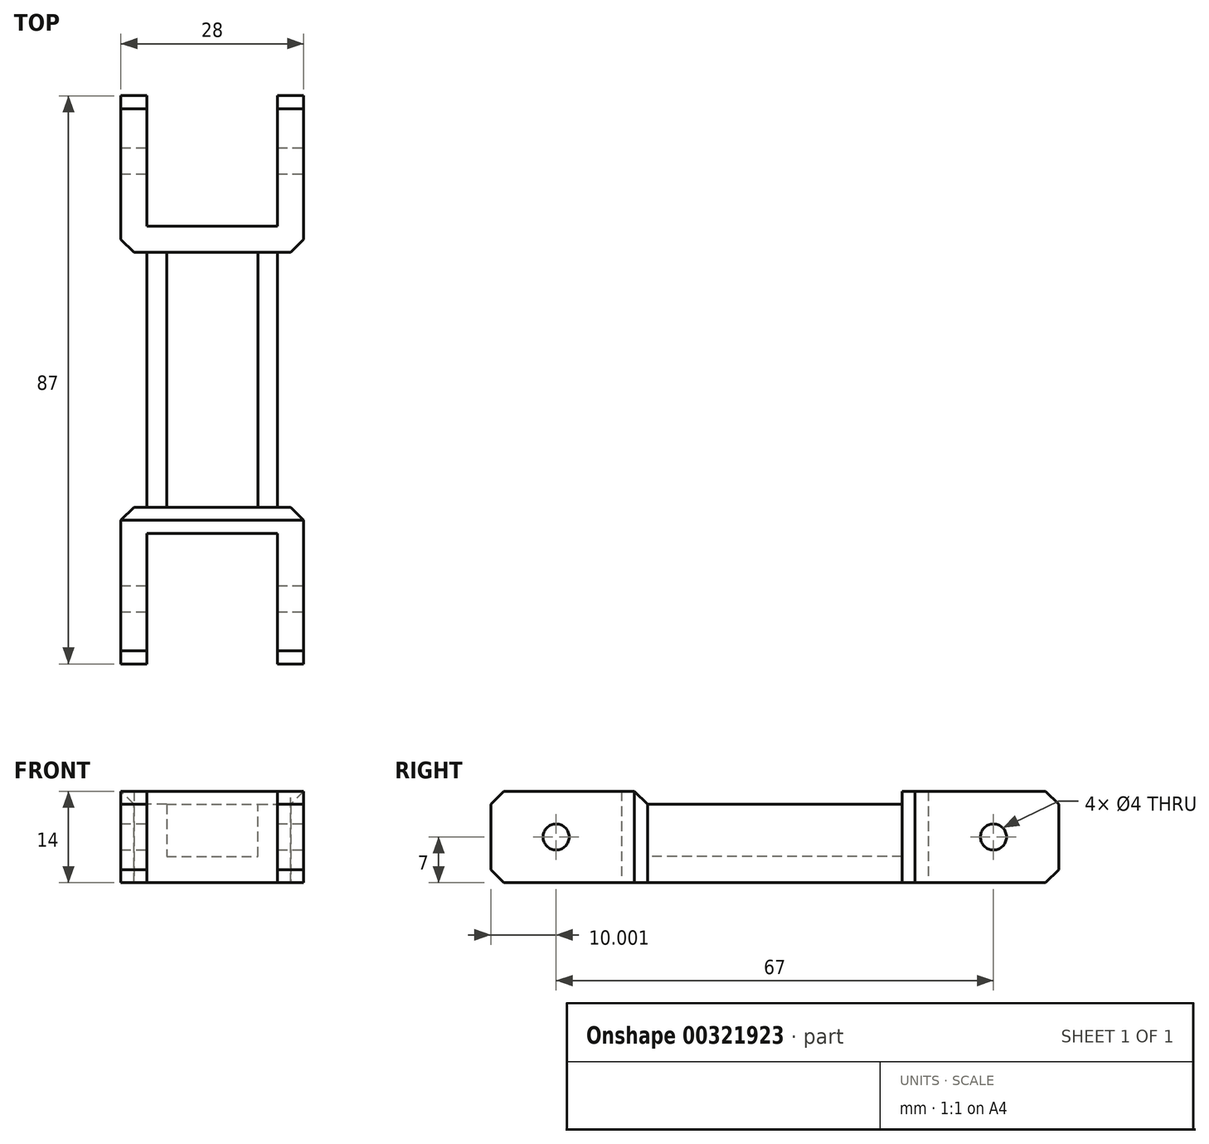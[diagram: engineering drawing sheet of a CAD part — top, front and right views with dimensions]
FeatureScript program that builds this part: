
annotation { "Feature Type Name" : "Feature", "Feature Type Description" : "" }
export const myFeature = defineFeature(function(context is Context, id is Id, definition is map)
    precondition{}
    {
        {
            var Q0;
            Q0=qCreatedBy(makeId("Top.planeOp"),FACE);
            var sketch = newSketch(context, id + "F0", { "sketchPlane" : qUnion([Q0])});
            skLineSegment(sketch, "E0.bottom", {"start": v(-54.4, 33.69) * mm, "end": v(-34.4, 33.69) * mm});
            skLineSegment(sketch, "E0.top", {"start": v(-54.4, 13.29) * mm, "end": v(-34.4, 13.29) * mm});
            skLineSegment(sketch, "E0.left", {"start": v(-54.4, 33.69) * mm, "end": v(-54.4, 13.29) * mm});
            skLineSegment(sketch, "E0.right", {"start": v(-34.4, 33.69) * mm, "end": v(-34.4, 13.29) * mm});
            skLineSegment(sketch, "E1.bottom", {"start": v(-54.4, 63.69) * mm, "end": v(-34.4, 63.69) * mm});
            skLineSegment(sketch, "E1.top", {"start": v(-54.4, 9.29) * mm, "end": v(-34.4, 9.29) * mm});
            skLineSegment(sketch, "E1.left", {"start": v(-54.4, 63.69) * mm, "end": v(-54.4, 9.29) * mm});
            skLineSegment(sketch, "E1.right", {"start": v(-34.4, 63.69) * mm, "end": v(-34.4, 9.29) * mm});
            skLineSegment(sketch, "E2", {"start": v(-54.4, 59.69) * mm, "end": v(-34.4, 59.69) * mm});
            skLineSegment(sketch, "E3", {"start": v(-54.4, 37.69) * mm, "end": v(-34.4, 37.69) * mm});
            skSolve(sketch);
        }
        {
            var Q0;
            {var subQ0=sQuery(id+"F0.wireOp",EDGE,"E2");Q0=makeQuery(id+"F0.imprint","IMPRINT",FACE,{"disambiguationData":[TD([[makeQuery(id+"F0.imprint","IMPRINT",EDGE,{"derivedFrom":subQ0}),-1.0]])]});}
            var Q1;
            {var subQ0=sQuery(id+"F0.wireOp",EDGE,"E1.bottom");Q1=makeQuery(id+"F0.imprint","IMPRINT",FACE,{"disambiguationData":[TD([[makeQuery(id+"F0.imprint","IMPRINT",EDGE,{"derivedFrom":subQ0}),-1.0]])]});}
            var Q2;
            Q2=makeQuery(id+"F0.imprint","IMPRINT",FACE,{"disambiguationData":[TD([[makeQuery(id+"F0.imprint","IMPRINT",EDGE,{"derivedFrom":sQuery(id+"F0.wireOp",EDGE,"E0.bottom")}),1.0]])]});
            var Q3;
            {var subQ0=sQuery(id+"F0.wireOp",EDGE,"E0.bottom");Q3=makeQuery(id+"F0.imprint","IMPRINT",FACE,{"disambiguationData":[TD([[makeQuery(id+"F0.imprint","IMPRINT",EDGE,{"derivedFrom":subQ0}),-1.0]])]});}
            var Q4;
            {var subQ0=sQuery(id+"F0.wireOp",EDGE,"E0.top");Q4=makeQuery(id+"F0.imprint","IMPRINT",FACE,{"disambiguationData":[TD([[makeQuery(id+"F0.imprint","IMPRINT",EDGE,{"derivedFrom":subQ0}),-1.0]])]});}
            extrude(context, id + "F1", {"entities" : qUnion([Q0, Q1, Q2, Q3, Q4]), "oppositeDirection" : true, "depth" : 2 * mm});
        }
        {
            var Q0;
            Q0=makeQuery(id+"F0.imprint","IMPRINT",FACE,{"disambiguationData":[TD([[makeQuery(id+"F0.imprint","IMPRINT",EDGE,{"derivedFrom":sQuery(id+"F0.wireOp",EDGE,"E0.bottom")}),1.0]])]});
            var Q1;
            {var subQ0=sQuery(id+"F0.wireOp",EDGE,"E1.bottom");Q1=makeQuery(id+"F0.imprint","IMPRINT",FACE,{"disambiguationData":[TD([[makeQuery(id+"F0.imprint","IMPRINT",EDGE,{"derivedFrom":subQ0}),-1.0]])]});}
            var Q2;
            {var subQ0=sQuery(id+"F0.wireOp",EDGE,"E0.top");Q2=makeQuery(id+"F0.imprint","IMPRINT",FACE,{"disambiguationData":[TD([[makeQuery(id+"F0.imprint","IMPRINT",EDGE,{"derivedFrom":subQ0}),-1.0]])]});}
            extrude(context, id + "F2", {"entities" : qUnion([Q0, Q1, Q2]), "operationType" : NewBodyOperationType.ADD, "depth" : 10 * mm});
        }
        {
            var Q0;
            {var subQ0=sQuery(id+"F0.wireOp",EDGE,"E1.top");Q0=makeQuery(id+"F2.boolean.opBoolean","MERGE",FACE,{"derivedFrom":[makeQuery(id+"F1.opExtrude","SWEPT_FACE",FACE,{"disambiguationData":[OSD([subQ0])]}),makeQuery(id+"F2.opExtrude","SWEPT_FACE",FACE,{"disambiguationData":[OSD([subQ0])]})]});}
            var sketch = newSketch(context, id + "F3", { "sketchPlane" : qUnion([Q0])});
            skCircle(sketch, "E4", {"center": v(-44.4, 5.5) * mm, "radius": 2.2 * mm});
            skPoint(sketch, "E4.centerSnap0", {"position": v(-44.4, -2) * mm});
            skSolve(sketch);
        }
        {
            var Q0;
            Q0=makeQuery(id+"F3.imprint","IMPRINT",FACE,{"disambiguationData":[TD([[makeQuery(id+"F3.imprint","IMPRINT",EDGE,{"derivedFrom":sQuery(id+"F3.wireOp",EDGE,"E4")}),1.0]])]});
            extrude(context, id + "F4", {"entities" : qUnion([Q0]), "operationType" : NewBodyOperationType.REMOVE, "oppositeDirection" : true, "depth" : 30 * mm, "offsetDistance" : 25 * mm});
        }
        {
            var Q0;
            {var subQ0=sQuery(id+"F0.wireOp",EDGE,"E1.left");Q0=makeQuery(id+"F2.boolean.opBoolean","MERGE",FACE,{"derivedFrom":[makeQuery(id+"F1.opExtrude","SWEPT_FACE",FACE,{"disambiguationData":[OSD([subQ0])]}),makeQuery(id+"F2.opExtrude","SWEPT_FACE",FACE,{"disambiguationData":[OSD([subQ0]),TDD([makeQuery(id+"F0.imprint","IMPRINT",EDGE,{"disambiguationData":[TD([[makeQuery(id+"F0.imprint","INTERSECT",VERTEX,{"derivedFrom":[sQuery(id+"F0.wireOp",EDGE,"E1.bottom"),subQ0]}),-1.0]])],"derivedFrom":subQ0})])]}),makeQuery(id+"F2.opExtrude","SWEPT_FACE",FACE,{"disambiguationData":[OSD([subQ0]),TDD([makeQuery(id+"F0.imprint","IMPRINT",EDGE,{"disambiguationData":[TD([[makeQuery(id+"F0.imprint","INTERSECT",VERTEX,{"derivedFrom":[sQuery(id+"F0.wireOp",EDGE,"E0.bottom"),subQ0]}),1.0]])],"derivedFrom":subQ0})])]}),makeQuery(id+"F2.opExtrude","SWEPT_FACE",FACE,{"disambiguationData":[OSD([subQ0]),TDD([makeQuery(id+"F0.imprint","IMPRINT",EDGE,{"disambiguationData":[TD([[makeQuery(id+"F0.imprint","INTERSECT",VERTEX,{"derivedFrom":[sQuery(id+"F0.wireOp",EDGE,"E0.top"),subQ0]}),-1.0]])],"derivedFrom":subQ0})])]})]});}
            var sketch = newSketch(context, id + "F5", { "sketchPlane" : qUnion([Q0])});
            skLineSegment(sketch, "E5.bottom", {"start": v(-59.69, 10) * mm, "end": v(-83.69, 10) * mm});
            skLineSegment(sketch, "E5.top", {"start": v(-59.69, -2) * mm, "end": v(-83.69, -2) * mm});
            skLineSegment(sketch, "E5.left", {"start": v(-59.69, 10) * mm, "end": v(-59.69, -2) * mm});
            skLineSegment(sketch, "E5.right", {"start": v(-83.69, 10) * mm, "end": v(-83.69, -2) * mm});
            skCircle(sketch, "E6", {"center": v(-73.69, 4) * mm, "radius": 2.6 * mm});
            skPoint(sketch, "E6.centerSnap0", {"position": v(-83.69, 4) * mm});
            skSolve(sketch);
        }
        {
            var Q0;
            {var subQ0=sQuery(id+"F0.wireOp",EDGE,"E1.right");Q0=makeQuery(id+"F2.boolean.opBoolean","MERGE",FACE,{"derivedFrom":[makeQuery(id+"F1.opExtrude","SWEPT_FACE",FACE,{"disambiguationData":[OSD([subQ0])]}),makeQuery(id+"F2.opExtrude","SWEPT_FACE",FACE,{"disambiguationData":[OSD([subQ0]),TDD([makeQuery(id+"F0.imprint","IMPRINT",EDGE,{"disambiguationData":[TD([[makeQuery(id+"F0.imprint","INTERSECT",VERTEX,{"derivedFrom":[sQuery(id+"F0.wireOp",EDGE,"E1.bottom"),subQ0]}),-1.0]])],"derivedFrom":subQ0})])]}),makeQuery(id+"F2.opExtrude","SWEPT_FACE",FACE,{"disambiguationData":[OSD([subQ0]),TDD([makeQuery(id+"F0.imprint","IMPRINT",EDGE,{"disambiguationData":[TD([[makeQuery(id+"F0.imprint","INTERSECT",VERTEX,{"derivedFrom":[sQuery(id+"F0.wireOp",EDGE,"E0.bottom"),subQ0]}),1.0]])],"derivedFrom":subQ0})])]}),makeQuery(id+"F2.opExtrude","SWEPT_FACE",FACE,{"disambiguationData":[OSD([subQ0]),TDD([makeQuery(id+"F0.imprint","IMPRINT",EDGE,{"disambiguationData":[TD([[makeQuery(id+"F0.imprint","INTERSECT",VERTEX,{"derivedFrom":[sQuery(id+"F0.wireOp",EDGE,"E0.top"),subQ0]}),-1.0]])],"derivedFrom":subQ0})])]})]});}
            var sketch = newSketch(context, id + "F6", { "sketchPlane" : qUnion([Q0])});
            skLineSegment(sketch, "E7.bottom", {"start": v(59.69, 10) * mm, "end": v(83.69, 10) * mm});
            skLineSegment(sketch, "E7.top", {"start": v(59.69, -2) * mm, "end": v(83.69, -2) * mm});
            skLineSegment(sketch, "E7.left", {"start": v(59.69, 10) * mm, "end": v(59.69, -2) * mm});
            skLineSegment(sketch, "E7.right", {"start": v(83.69, 10) * mm, "end": v(83.69, -2) * mm});
            skCircle(sketch, "E8", {"center": v(73.69, 4) * mm, "radius": 2.6 * mm});
            skPoint(sketch, "E8.centerSnap0", {"position": v(83.69, 4) * mm});
            skSolve(sketch);
        }
        {
            var Q0;
            {var subQ4=sQuery(id+"F5.wireOp",EDGE,"E5.right");Q0=makeQuery(id+"F5.imprint","IMPRINT",FACE,{"disambiguationData":[TD([[makeQuery(id+"F5.imprint","IMPRINT",EDGE,{"derivedFrom":subQ4}),1.0]])]});}
            var Q1;
            {var subQ3=sQuery(id+"F0.wireOp",EDGE,"E1.left");var subQ5=sQuery(id+"F0.wireOp",EDGE,"E1.bottom");var subQ10=makeQuery(id+"F2.boolean.opBoolean","MERGE",EDGE,{"derivedFrom":[makeQuery(id+"F1.opExtrude","SWEPT_EDGE",EDGE,{"disambiguationData":[OSD([subQ5,subQ3])]}),makeQuery(id+"F2.opExtrude","SWEPT_EDGE",EDGE,{"disambiguationData":[OSD([subQ5,subQ3])]})]});Q1=makeQuery(id+"F5.imprint","IMPRINT",FACE,{"disambiguationData":[TD([[makeQuery(id+"F5.imprint","IMPRINT",EDGE,{"derivedFrom":subQ10}),-1.0]])]});}
            extrude(context, id + "F7", {"entities" : qUnion([Q0, Q1]), "operationType" : NewBodyOperationType.ADD, "depth" : 4 * mm});
        }
        {
            var Q0;
            {var subQ0=sQuery(id+"F5.wireOp",EDGE,"As3iJ9jp-MM02-xgW6-gQvA-6wpTA8jTOXIw.right");Q0=makeQuery(id+"F5.imprint","IMPRINT",FACE,{"disambiguationData":[TD([[makeQuery(id+"F5.imprint","IMPRINT",EDGE,{"derivedFrom":subQ0}),-1.0]])]});}
            var Q1;
            {var subQ5=sQuery(id+"F5.wireOp",EDGE,"D0sxENBk-QWaU-MoL9-KmcH-z9rnvNsLjtkH");Q1=makeQuery(id+"F5.imprint","IMPRINT",FACE,{"disambiguationData":[TD([[makeQuery(id+"F5.imprint","IMPRINT",EDGE,{"derivedFrom":subQ5}),-1.0]])]});}
            var Q2;
            {var subQ4=sQuery(id+"F6.wireOp",EDGE,"E7.right");Q2=makeQuery(id+"F6.imprint","IMPRINT",FACE,{"disambiguationData":[TD([[makeQuery(id+"F6.imprint","IMPRINT",EDGE,{"derivedFrom":subQ4}),-1.0]])]});}
            var Q3;
            {var subQ3=sQuery(id+"F0.wireOp",EDGE,"E1.right");var subQ4=sQuery(id+"F0.wireOp",EDGE,"E1.bottom");var subQ10=makeQuery(id+"F2.boolean.opBoolean","MERGE",EDGE,{"derivedFrom":[makeQuery(id+"F1.opExtrude","SWEPT_EDGE",EDGE,{"disambiguationData":[OSD([subQ4,subQ3])]}),makeQuery(id+"F2.opExtrude","SWEPT_EDGE",EDGE,{"disambiguationData":[OSD([subQ4,subQ3])]})]});Q3=makeQuery(id+"F6.imprint","IMPRINT",FACE,{"disambiguationData":[TD([[makeQuery(id+"F6.imprint","IMPRINT",EDGE,{"derivedFrom":subQ10}),1.0]])]});}
            extrude(context, id + "F8", {"entities" : qUnion([Q0, Q1, Q2, Q3]), "operationType" : NewBodyOperationType.ADD, "depth" : 4 * mm});
        }
        {
            var Q0;
            Q0=makeQuery(id+"F8.boolean.opBoolean","MERGE",FACE,{"derivedFrom":[makeQuery(id+"F7.boolean.opBoolean","MERGE",FACE,{"derivedFrom":[makeQuery(id+"F1.opExtrude","CAP_FACE",FACE,{"disambiguationData":[OSD([sQuery(id+"F0.wireOp",EDGE,"E1.bottom"),sQuery(id+"F0.wireOp",EDGE,"E1.top"),sQuery(id+"F0.wireOp",EDGE,"E1.left"),sQuery(id+"F0.wireOp",EDGE,"E1.right")])],"isStart":false}),makeQuery(id+"F7.opExtrude","SWEPT_FACE",FACE,{"disambiguationData":[OSD([sQuery(id+"F5.wireOp",EDGE,"E5.top")])]})]}),makeQuery(id+"F8.opExtrude","SWEPT_FACE",FACE,{"disambiguationData":[OSD([sQuery(id+"F6.wireOp",EDGE,"E7.top")])]})]});
            var Q1;
            Q1=makeQuery(id+"F8.boolean.opBoolean","MERGE",FACE,{"derivedFrom":[makeQuery(id+"F7.boolean.opBoolean","MERGE",FACE,{"derivedFrom":[makeQuery(id+"F2.opExtrude","CAP_FACE",FACE,{"disambiguationData":[OSD([sQuery(id+"F0.wireOp",EDGE,"E1.bottom"),sQuery(id+"F0.wireOp",EDGE,"E1.left"),sQuery(id+"F0.wireOp",EDGE,"E1.right"),sQuery(id+"F0.wireOp",EDGE,"E2")])],"isStart":false}),makeQuery(id+"F7.opExtrude","SWEPT_FACE",FACE,{"disambiguationData":[OSD([sQuery(id+"F5.wireOp",EDGE,"E5.bottom")])]})]}),makeQuery(id+"F8.opExtrude","SWEPT_FACE",FACE,{"disambiguationData":[OSD([sQuery(id+"F6.wireOp",EDGE,"E7.bottom")])]})]});
            var Q2;
            Q2=makeQuery(id+"F2.opExtrude","CAP_FACE",FACE,{"disambiguationData":[OSD([sQuery(id+"F0.wireOp",EDGE,"E0.bottom"),sQuery(id+"F0.wireOp",EDGE,"E1.left"),sQuery(id+"F0.wireOp",EDGE,"E1.right"),sQuery(id+"F0.wireOp",EDGE,"E3")])],"isStart":false});
            var Q3;
            Q3=makeQuery(id+"F2.opExtrude","CAP_FACE",FACE,{"disambiguationData":[OSD([sQuery(id+"F0.wireOp",EDGE,"E0.top"),sQuery(id+"F0.wireOp",EDGE,"E1.top"),sQuery(id+"F0.wireOp",EDGE,"E1.left"),sQuery(id+"F0.wireOp",EDGE,"E1.right")])],"isStart":false});
            var Q4;
            {var subQ0=sQuery(id+"F0.wireOp",EDGE,"E1.right");var subQ1=sQuery(id+"F0.wireOp",EDGE,"E1.top");Q4=makeQuery(id+"F2.boolean.opBoolean","MERGE",EDGE,{"derivedFrom":[makeQuery(id+"F1.opExtrude","SWEPT_EDGE",EDGE,{"disambiguationData":[OSD([subQ1,subQ0])]}),makeQuery(id+"F2.opExtrude","SWEPT_EDGE",EDGE,{"disambiguationData":[OSD([subQ1,subQ0])]})]});}
            var Q5;
            {var subQ0=sQuery(id+"F0.wireOp",EDGE,"E1.left");var subQ1=sQuery(id+"F0.wireOp",EDGE,"E1.top");Q5=makeQuery(id+"F2.boolean.opBoolean","MERGE",EDGE,{"derivedFrom":[makeQuery(id+"F1.opExtrude","SWEPT_EDGE",EDGE,{"disambiguationData":[OSD([subQ1,subQ0])]}),makeQuery(id+"F2.opExtrude","SWEPT_EDGE",EDGE,{"disambiguationData":[OSD([subQ1,subQ0])]})]});}
            var Q6;
            Q6=makeQuery(id+"F7.opExtrude","CAP_EDGE",EDGE,{"disambiguationData":[OSD([sQuery(id+"F5.wireOp",EDGE,"E5.left")])],"isStart":false});
            var Q7;
            Q7=makeQuery(id+"F8.opExtrude","CAP_EDGE",EDGE,{"disambiguationData":[OSD([sQuery(id+"F6.wireOp",EDGE,"E7.left")])],"isStart":false});
            var Q8;
            Q8=makeQuery(id+"F8.opExtrude","CAP_EDGE",EDGE,{"disambiguationData":[OSD([sQuery(id+"F6.wireOp",EDGE,"E7.right")])],"isStart":false});
            var Q9;
            Q9=makeQuery(id+"F7.opExtrude","CAP_EDGE",EDGE,{"disambiguationData":[OSD([sQuery(id+"F5.wireOp",EDGE,"E5.right")])],"isStart":false});
            fillet(context, id + "F9", {"entities" : qUnion([Q0, Q1, Q2, Q3, Q4, Q5, Q6, Q7, Q8, Q9]), "radius" : 2 * mm, "allowEdgeOverflow" : false});
        }
        {
            var Q0;
            Q0=qCreatedBy(makeId("Top.planeOp"),FACE);
            var sketch = newSketch(context, id + "F10", { "sketchPlane" : qUnion([Q0])});
            skLineSegment(sketch, "E9.bottom", {"start": v(-54.07, -34.84) * mm, "end": v(-34.07, -34.84) * mm});
            skLineSegment(sketch, "E9.top", {"start": v(-54.07, -81.84) * mm, "end": v(-34.07, -81.84) * mm});
            skLineSegment(sketch, "E9.left", {"start": v(-54.07, -34.84) * mm, "end": v(-54.07, -81.84) * mm});
            skLineSegment(sketch, "E9.right", {"start": v(-34.07, -34.84) * mm, "end": v(-34.07, -81.84) * mm});
            skSolve(sketch);
        }
        {
            var Q0;
            Q0 = qSketchRegion(id + "F10", true);
            extrude(context, id + "F11", {"entities" : qUnion([Q0]), "depth" : 4 * mm, "offsetDistance" : 25 * mm});
        }
        {
            var Q0;
            Q0=makeQuery(id+"F11.opExtrude","CAP_FACE",FACE,{"disambiguationData":[OSD([sQuery(id+"F10.wireOp",EDGE,"E9.bottom"),sQuery(id+"F10.wireOp",EDGE,"E9.top"),sQuery(id+"F10.wireOp",EDGE,"E9.left"),sQuery(id+"F10.wireOp",EDGE,"E9.right")])],"isStart":false});
            var sketch = newSketch(context, id + "F12", { "sketchPlane" : qUnion([Q0])});
            skLineSegment(sketch, "E10", {"start": v(-54.07, -38.84) * mm, "end": v(-34.07, -38.84) * mm});
            skLineSegment(sketch, "E11", {"start": v(-54.07, -77.84) * mm, "end": v(-34.07, -77.84) * mm});
            skSolve(sketch);
        }
        {
            var Q0;
            {var subQ0=sQuery(id+"F12.wireOp",EDGE,"E10");Q0=makeQuery(id+"F12.imprint","IMPRINT",FACE,{"disambiguationData":[TD([[makeQuery(id+"F12.imprint","IMPRINT",EDGE,{"derivedFrom":subQ0}),1.0]])]});}
            var Q1;
            {var subQ0=sQuery(id+"F12.wireOp",EDGE,"E11");Q1=makeQuery(id+"F12.imprint","IMPRINT",FACE,{"disambiguationData":[TD([[makeQuery(id+"F12.imprint","IMPRINT",EDGE,{"derivedFrom":subQ0}),-1.0]])]});}
            extrude(context, id + "F13", {"entities" : qUnion([Q0, Q1]), "operationType" : NewBodyOperationType.ADD, "depth" : 10 * mm, "offsetDistance" : 25 * mm});
        }
        {
            var Q0;
            {var subQ0=sQuery(id+"F10.wireOp",EDGE,"E9.left");var subQ1=makeQuery(id+"F11.opExtrude","CAP_EDGE",EDGE,{"disambiguationData":[OSD([subQ0])],"isStart":false});Q0=makeQuery(id+"F13.boolean.opBoolean","MERGE",FACE,{"derivedFrom":[makeQuery(id+"F11.opExtrude","SWEPT_FACE",FACE,{"disambiguationData":[OSD([subQ0])]}),makeQuery(id+"F13.opExtrude","SWEPT_FACE",FACE,{"disambiguationData":[OSD([subQ0]),TDD([makeQuery(id+"F12.imprint","IMPRINT",EDGE,{"disambiguationData":[TD([[makeQuery(id+"F12.imprint","INTERSECT",VERTEX,{"derivedFrom":[makeQuery(id+"F11.opExtrude","CAP_EDGE",EDGE,{"disambiguationData":[OSD([sQuery(id+"F10.wireOp",EDGE,"E9.bottom")])],"isStart":false}),subQ1]}),-1.0]])],"derivedFrom":subQ1})])]}),makeQuery(id+"F13.opExtrude","SWEPT_FACE",FACE,{"disambiguationData":[OSD([subQ0]),TDD([makeQuery(id+"F12.imprint","IMPRINT",EDGE,{"disambiguationData":[TD([[makeQuery(id+"F12.imprint","INTERSECT",VERTEX,{"derivedFrom":[makeQuery(id+"F11.opExtrude","CAP_EDGE",EDGE,{"disambiguationData":[OSD([sQuery(id+"F10.wireOp",EDGE,"E9.top")])],"isStart":false}),subQ1]}),1.0]])],"derivedFrom":subQ1})])]})]});}
            var sketch = newSketch(context, id + "F14", { "sketchPlane" : qUnion([Q0])});
            skLineSegment(sketch, "E12", {"start": v(38.84, 4) * mm, "end": v(38.84, 0) * mm});
            skLineSegment(sketch, "E13", {"start": v(77.84, 4) * mm, "end": v(77.84, 0) * mm});
            skSolve(sketch);
        }
        {
            var Q0;
            {var subQ0=sQuery(id+"F10.wireOp",EDGE,"E9.right");var subQ1=makeQuery(id+"F11.opExtrude","CAP_EDGE",EDGE,{"disambiguationData":[OSD([subQ0])],"isStart":false});Q0=makeQuery(id+"F13.boolean.opBoolean","MERGE",FACE,{"derivedFrom":[makeQuery(id+"F11.opExtrude","SWEPT_FACE",FACE,{"disambiguationData":[OSD([subQ0])]}),makeQuery(id+"F13.opExtrude","SWEPT_FACE",FACE,{"disambiguationData":[OSD([subQ0]),TDD([makeQuery(id+"F12.imprint","IMPRINT",EDGE,{"disambiguationData":[TD([[makeQuery(id+"F12.imprint","INTERSECT",VERTEX,{"derivedFrom":[makeQuery(id+"F11.opExtrude","CAP_EDGE",EDGE,{"disambiguationData":[OSD([sQuery(id+"F10.wireOp",EDGE,"E9.bottom")])],"isStart":false}),subQ1]}),-1.0]])],"derivedFrom":subQ1})])]}),makeQuery(id+"F13.opExtrude","SWEPT_FACE",FACE,{"disambiguationData":[OSD([subQ0]),TDD([makeQuery(id+"F12.imprint","IMPRINT",EDGE,{"disambiguationData":[TD([[makeQuery(id+"F12.imprint","INTERSECT",VERTEX,{"derivedFrom":[makeQuery(id+"F11.opExtrude","CAP_EDGE",EDGE,{"disambiguationData":[OSD([sQuery(id+"F10.wireOp",EDGE,"E9.top")])],"isStart":false}),subQ1]}),1.0]])],"derivedFrom":subQ1})])]})]});}
            var sketch = newSketch(context, id + "F15", { "sketchPlane" : qUnion([Q0])});
            skLineSegment(sketch, "E14", {"start": v(-77.84, 4) * mm, "end": v(-77.84, 0) * mm});
            skLineSegment(sketch, "E15", {"start": v(-38.84, 4) * mm, "end": v(-38.84, 0) * mm});
            skSolve(sketch);
        }
        {
            var Q0;
            {var subQ5=sQuery(id+"F15.wireOp",EDGE,"E14");Q0=makeQuery(id+"F15.imprint","IMPRINT",FACE,{"disambiguationData":[TD([[makeQuery(id+"F15.imprint","IMPRINT",EDGE,{"derivedFrom":subQ5}),-1.0]])]});}
            var Q1;
            {var subQ5=sQuery(id+"F15.wireOp",EDGE,"E15");Q1=makeQuery(id+"F15.imprint","IMPRINT",FACE,{"disambiguationData":[TD([[makeQuery(id+"F15.imprint","IMPRINT",EDGE,{"derivedFrom":subQ5}),1.0]])]});}
            extrude(context, id + "F16", {"entities" : qUnion([Q0, Q1]), "operationType" : NewBodyOperationType.ADD, "depth" : 4 * mm, "offsetDistance" : 25 * mm});
        }
        {
            var Q0;
            {var subQ5=sQuery(id+"F14.wireOp",EDGE,"E12");Q0=makeQuery(id+"F14.imprint","IMPRINT",FACE,{"disambiguationData":[TD([[makeQuery(id+"F14.imprint","IMPRINT",EDGE,{"derivedFrom":subQ5}),-1.0]])]});}
            var Q1;
            {var subQ5=sQuery(id+"F14.wireOp",EDGE,"E13");Q1=makeQuery(id+"F14.imprint","IMPRINT",FACE,{"disambiguationData":[TD([[makeQuery(id+"F14.imprint","IMPRINT",EDGE,{"derivedFrom":subQ5}),1.0]])]});}
            extrude(context, id + "F17", {"entities" : qUnion([Q0, Q1]), "operationType" : NewBodyOperationType.ADD, "depth" : 4 * mm, "offsetDistance" : 25 * mm});
        }
        {
            var Q0;
            {var subQ0=sQuery(id+"F10.wireOp",EDGE,"E9.bottom");Q0=makeQuery(id+"F17.boolean.opBoolean","MERGE",FACE,{"derivedFrom":[makeQuery(id+"F16.boolean.opBoolean","MERGE",FACE,{"derivedFrom":[makeQuery(id+"F13.boolean.opBoolean","MERGE",FACE,{"derivedFrom":[makeQuery(id+"F11.opExtrude","SWEPT_FACE",FACE,{"disambiguationData":[OSD([subQ0])]}),makeQuery(id+"F13.opExtrude","SWEPT_FACE",FACE,{"disambiguationData":[OSD([subQ0])]})]}),makeQuery(id+"F16.opExtrude","SWEPT_FACE",FACE,{"disambiguationData":[OSD([subQ0,sQuery(id+"F10.wireOp",EDGE,"E9.right")])]})]}),makeQuery(id+"F17.opExtrude","SWEPT_FACE",FACE,{"disambiguationData":[OSD([subQ0,sQuery(id+"F10.wireOp",EDGE,"E9.left")])]})]});}
            var sketch = newSketch(context, id + "F18", { "sketchPlane" : qUnion([Q0])});
            skLineSegment(sketch, "E16", {"start": v(34.07, 14) * mm, "end": v(34.07, 0) * mm});
            skLineSegment(sketch, "E17", {"start": v(54.07, 14) * mm, "end": v(54.07, 0) * mm});
            skSolve(sketch);
        }
        {
            var Q0;
            {var subQ0=sQuery(id+"F10.wireOp",EDGE,"E9.top");Q0=makeQuery(id+"F17.boolean.opBoolean","MERGE",FACE,{"derivedFrom":[makeQuery(id+"F16.boolean.opBoolean","MERGE",FACE,{"derivedFrom":[makeQuery(id+"F13.boolean.opBoolean","MERGE",FACE,{"derivedFrom":[makeQuery(id+"F11.opExtrude","SWEPT_FACE",FACE,{"disambiguationData":[OSD([subQ0])]}),makeQuery(id+"F13.opExtrude","SWEPT_FACE",FACE,{"disambiguationData":[OSD([subQ0])]})]}),makeQuery(id+"F16.opExtrude","SWEPT_FACE",FACE,{"disambiguationData":[OSD([subQ0,sQuery(id+"F10.wireOp",EDGE,"E9.right")])]})]}),makeQuery(id+"F17.opExtrude","SWEPT_FACE",FACE,{"disambiguationData":[OSD([subQ0,sQuery(id+"F10.wireOp",EDGE,"E9.left")])]})]});}
            var sketch = newSketch(context, id + "F19", { "sketchPlane" : qUnion([Q0])});
            skLineSegment(sketch, "E18", {"start": v(-54.07, 14) * mm, "end": v(-54.07, 0) * mm});
            skLineSegment(sketch, "E19", {"start": v(-34.07, 14) * mm, "end": v(-34.07, 0) * mm});
            skSolve(sketch);
        }
        {
            var Q0;
            {var subQ0=sQuery(id+"F19.wireOp",EDGE,"E18");Q0=makeQuery(id+"F19.imprint","IMPRINT",FACE,{"disambiguationData":[TD([[makeQuery(id+"F19.imprint","IMPRINT",EDGE,{"derivedFrom":subQ0}),-1.0]])]});}
            var Q1;
            {var subQ0=sQuery(id+"F19.wireOp",EDGE,"E19");Q1=makeQuery(id+"F19.imprint","IMPRINT",FACE,{"disambiguationData":[TD([[makeQuery(id+"F19.imprint","IMPRINT",EDGE,{"derivedFrom":subQ0}),1.0]])]});}
            extrude(context, id + "F20", {"entities" : qUnion([Q0, Q1]), "operationType" : NewBodyOperationType.ADD, "depth" : 20 * mm, "offsetDistance" : 25 * mm});
        }
        {
            var Q0;
            {var subQ0=sQuery(id+"F18.wireOp",EDGE,"E16");Q0=makeQuery(id+"F18.imprint","IMPRINT",FACE,{"disambiguationData":[TD([[makeQuery(id+"F18.imprint","IMPRINT",EDGE,{"derivedFrom":subQ0}),-1.0]])]});}
            var Q1;
            {var subQ0=sQuery(id+"F18.wireOp",EDGE,"E17");Q1=makeQuery(id+"F18.imprint","IMPRINT",FACE,{"disambiguationData":[TD([[makeQuery(id+"F18.imprint","IMPRINT",EDGE,{"derivedFrom":subQ0}),1.0]])]});}
            extrude(context, id + "F21", {"entities" : qUnion([Q0, Q1]), "operationType" : NewBodyOperationType.ADD, "depth" : 20 * mm, "offsetDistance" : 25 * mm});
        }
        {
            var Q0;
            {var subQ0=sQuery(id+"F10.wireOp",EDGE,"E9.left");var subQ1=makeQuery(id+"F11.opExtrude","CAP_EDGE",EDGE,{"disambiguationData":[OSD([subQ0])],"isStart":false});Q0=makeQuery(id+"F13.boolean.opBoolean","MERGE",FACE,{"derivedFrom":[makeQuery(id+"F11.opExtrude","SWEPT_FACE",FACE,{"disambiguationData":[OSD([subQ0])]}),makeQuery(id+"F13.opExtrude","SWEPT_FACE",FACE,{"disambiguationData":[OSD([subQ0]),TDD([makeQuery(id+"F12.imprint","IMPRINT",EDGE,{"disambiguationData":[TD([[makeQuery(id+"F12.imprint","INTERSECT",VERTEX,{"derivedFrom":[makeQuery(id+"F11.opExtrude","CAP_EDGE",EDGE,{"disambiguationData":[OSD([sQuery(id+"F10.wireOp",EDGE,"E9.bottom")])],"isStart":false}),subQ1]}),-1.0]])],"derivedFrom":subQ1})])]}),makeQuery(id+"F13.opExtrude","SWEPT_FACE",FACE,{"disambiguationData":[OSD([subQ0]),TDD([makeQuery(id+"F12.imprint","IMPRINT",EDGE,{"disambiguationData":[TD([[makeQuery(id+"F12.imprint","INTERSECT",VERTEX,{"derivedFrom":[makeQuery(id+"F11.opExtrude","CAP_EDGE",EDGE,{"disambiguationData":[OSD([sQuery(id+"F10.wireOp",EDGE,"E9.top")])],"isStart":false}),subQ1]}),1.0]])],"derivedFrom":subQ1})])]})]});}
            var sketch = newSketch(context, id + "F22", { "sketchPlane" : qUnion([Q0])});
            skLineSegment(sketch, "E20", {"start": v(38.84, 4) * mm, "end": v(38.84, 12) * mm});
            skLineSegment(sketch, "E21", {"start": v(38.84, 12) * mm, "end": v(77.84, 12) * mm});
            skLineSegment(sketch, "E22", {"start": v(77.84, 12) * mm, "end": v(77.84, 4) * mm});
            skLineSegment(sketch, "E23", {"start": v(77.84, 4) * mm, "end": v(38.84, 4) * mm});
            skSolve(sketch);
        }
        {
            var Q0;
            Q0=makeQuery(id+"F22.imprint","IMPRINT",FACE,{"disambiguationData":[TD([[makeQuery(id+"F22.imprint","IMPRINT",EDGE,{"derivedFrom":sQuery(id+"F22.wireOp",EDGE,"E20")}),-1.0]])]});
            extrude(context, id + "F23", {"entities" : qUnion([Q0]), "operationType" : NewBodyOperationType.ADD, "oppositeDirection" : true, "depth" : 3 * mm, "offsetDistance" : 25 * mm});
        }
        {
            var Q0;
            {var subQ0=sQuery(id+"F10.wireOp",EDGE,"E9.right");var subQ1=makeQuery(id+"F11.opExtrude","CAP_EDGE",EDGE,{"disambiguationData":[OSD([subQ0])],"isStart":false});Q0=makeQuery(id+"F13.boolean.opBoolean","MERGE",FACE,{"derivedFrom":[makeQuery(id+"F11.opExtrude","SWEPT_FACE",FACE,{"disambiguationData":[OSD([subQ0])]}),makeQuery(id+"F13.opExtrude","SWEPT_FACE",FACE,{"disambiguationData":[OSD([subQ0]),TDD([makeQuery(id+"F12.imprint","IMPRINT",EDGE,{"disambiguationData":[TD([[makeQuery(id+"F12.imprint","INTERSECT",VERTEX,{"derivedFrom":[makeQuery(id+"F11.opExtrude","CAP_EDGE",EDGE,{"disambiguationData":[OSD([sQuery(id+"F10.wireOp",EDGE,"E9.bottom")])],"isStart":false}),subQ1]}),-1.0]])],"derivedFrom":subQ1})])]}),makeQuery(id+"F13.opExtrude","SWEPT_FACE",FACE,{"disambiguationData":[OSD([subQ0]),TDD([makeQuery(id+"F12.imprint","IMPRINT",EDGE,{"disambiguationData":[TD([[makeQuery(id+"F12.imprint","INTERSECT",VERTEX,{"derivedFrom":[makeQuery(id+"F11.opExtrude","CAP_EDGE",EDGE,{"disambiguationData":[OSD([sQuery(id+"F10.wireOp",EDGE,"E9.top")])],"isStart":false}),subQ1]}),1.0]])],"derivedFrom":subQ1})])]})]});}
            var sketch = newSketch(context, id + "F24", { "sketchPlane" : qUnion([Q0])});
            skLineSegment(sketch, "E24", {"start": v(-77.84, 4) * mm, "end": v(-77.84, 12) * mm});
            skLineSegment(sketch, "E25", {"start": v(-77.84, 12) * mm, "end": v(-38.84, 12) * mm});
            skLineSegment(sketch, "E26", {"start": v(-38.84, 12) * mm, "end": v(-38.84, 4) * mm});
            skLineSegment(sketch, "E27", {"start": v(-38.84, 4) * mm, "end": v(-77.84, 4) * mm});
            skSolve(sketch);
        }
        {
            var Q0;
            Q0=makeQuery(id+"F24.imprint","IMPRINT",FACE,{"disambiguationData":[TD([[makeQuery(id+"F24.imprint","IMPRINT",EDGE,{"derivedFrom":sQuery(id+"F24.wireOp",EDGE,"E24")}),-1.0]])]});
            extrude(context, id + "F25", {"entities" : qUnion([Q0]), "operationType" : NewBodyOperationType.ADD, "oppositeDirection" : true, "depth" : 3 * mm, "offsetDistance" : 25 * mm});
        }
        {
            var Q0;
            {var subQ0=sQuery(id+"F10.wireOp",EDGE,"E9.right");var subQ1=sQuery(id+"F10.wireOp",EDGE,"E9.top");Q0=makeQuery(id+"F20.boolean.opBoolean","MERGE",FACE,{"derivedFrom":[makeQuery(id+"F16.opExtrude","CAP_FACE",FACE,{"disambiguationData":[OSD([subQ1,subQ0,sQuery(id+"F12.wireOp",EDGE,"E11"),sQuery(id+"F15.wireOp",EDGE,"E14")])],"isStart":false}),makeQuery(id+"F20.opExtrude","SWEPT_FACE",FACE,{"disambiguationData":[OSD([subQ1,subQ0])]})]});}
            var sketch = newSketch(context, id + "F26", { "sketchPlane" : qUnion([Q0])});
            skCircle(sketch, "E28", {"center": v(-91.84, 7) * mm, "radius": 2 * mm});
            skPoint(sketch, "E28.centerSnap0", {"position": v(-101.84, 7) * mm});
            skPoint(sketch, "E28.centerSnap1", {"position": v(-89.84, 14) * mm});
            skSolve(sketch);
        }
        {
            var Q0;
            {var subQ0=sQuery(id+"F10.wireOp",EDGE,"E9.right");var subQ1=sQuery(id+"F10.wireOp",EDGE,"E9.bottom");Q0=makeQuery(id+"F21.boolean.opBoolean","MERGE",FACE,{"derivedFrom":[makeQuery(id+"F16.opExtrude","CAP_FACE",FACE,{"disambiguationData":[OSD([subQ1,subQ0,sQuery(id+"F12.wireOp",EDGE,"E10"),sQuery(id+"F15.wireOp",EDGE,"E15")])],"isStart":false}),makeQuery(id+"F21.opExtrude","SWEPT_FACE",FACE,{"disambiguationData":[OSD([subQ1,subQ0])]})]});}
            var sketch = newSketch(context, id + "F27", { "sketchPlane" : qUnion([Q0])});
            skCircle(sketch, "E29", {"center": v(-24.84, 7) * mm, "radius": 2 * mm});
            skPoint(sketch, "E29.centerSnap0", {"position": v(-14.84, 7) * mm});
            skPoint(sketch, "E29.centerSnap1", {"position": v(-26.84, 14) * mm});
            skSolve(sketch);
        }
        {
            var Q0;
            Q0=makeQuery(id+"F26.imprint","IMPRINT",FACE,{"disambiguationData":[TD([[makeQuery(id+"F26.imprint","IMPRINT",EDGE,{"derivedFrom":sQuery(id+"F26.wireOp",EDGE,"E28")}),1.0]])]});
            var Q1;
            Q1=makeQuery(id+"F27.imprint","IMPRINT",FACE,{"disambiguationData":[TD([[makeQuery(id+"F27.imprint","IMPRINT",EDGE,{"derivedFrom":sQuery(id+"F27.wireOp",EDGE,"E29")}),1.0]])]});
            extrude(context, id + "F28", {"entities" : qUnion([Q0, Q1]), "operationType" : NewBodyOperationType.REMOVE, "endBound" : BoundingType.THROUGH_ALL, "oppositeDirection" : true, "depth" : 25 * mm, "offsetDistance" : 25 * mm});
        }
        {
            var Q0;
            {var subQ0=sQuery(id+"F10.wireOp",EDGE,"E9.left");var subQ1=sQuery(id+"F10.wireOp",EDGE,"E9.top");var subQ2=sQuery(id+"F10.wireOp",EDGE,"E9.right");var subQ3=makeQuery(id+"F17.boolean.opBoolean","MERGE",EDGE,{"derivedFrom":[makeQuery(id+"F16.boolean.opBoolean","MERGE",EDGE,{"derivedFrom":[makeQuery(id+"F11.opExtrude","CAP_EDGE",EDGE,{"disambiguationData":[OSD([subQ1])],"isStart":true}),makeQuery(id+"F16.opExtrude","SWEPT_EDGE",EDGE,{"disambiguationData":[OSD([subQ1,subQ2]),TDD([makeQuery(id+"F15.imprint","INTERSECT",VERTEX,{"derivedFrom":[makeQuery(id+"F11.opExtrude","CAP_EDGE",EDGE,{"disambiguationData":[OSD([subQ2])],"isStart":true}),makeQuery(id+"F13.boolean.opBoolean","MERGE",EDGE,{"derivedFrom":[makeQuery(id+"F11.opExtrude","SWEPT_EDGE",EDGE,{"disambiguationData":[OSD([subQ1,subQ2])]}),makeQuery(id+"F13.opExtrude","SWEPT_EDGE",EDGE,{"disambiguationData":[OSD([subQ1,subQ2])]})]})]})])]})]}),makeQuery(id+"F17.opExtrude","SWEPT_EDGE",EDGE,{"disambiguationData":[OSD([subQ1,subQ0]),TDD([makeQuery(id+"F14.imprint","INTERSECT",VERTEX,{"derivedFrom":[makeQuery(id+"F11.opExtrude","CAP_EDGE",EDGE,{"disambiguationData":[OSD([subQ0])],"isStart":true}),makeQuery(id+"F13.boolean.opBoolean","MERGE",EDGE,{"derivedFrom":[makeQuery(id+"F11.opExtrude","SWEPT_EDGE",EDGE,{"disambiguationData":[OSD([subQ1,subQ0])]}),makeQuery(id+"F13.opExtrude","SWEPT_EDGE",EDGE,{"disambiguationData":[OSD([subQ1,subQ0])]})]})]})])]})]});Q0=makeQuery(id+"F20.opExtrude","CAP_EDGE",EDGE,{"disambiguationData":[OSD([subQ1,subQ0,subQ2]),TDD([makeQuery(id+"F19.imprint","IMPRINT",EDGE,{"disambiguationData":[TD([[makeQuery(id+"F19.imprint","INTERSECT",VERTEX,{"derivedFrom":[subQ3,sQuery(id+"F19.wireOp",EDGE,"E19")]}),-1.0]])],"derivedFrom":subQ3})])],"isStart":false});}
            var Q1;
            Q1=makeQuery(id+"F16.opExtrude","CAP_EDGE",EDGE,{"disambiguationData":[OSD([sQuery(id+"F10.wireOp",EDGE,"E9.right"),sQuery(id+"F12.wireOp",EDGE,"E11"),sQuery(id+"F15.wireOp",EDGE,"E14")])],"isStart":false});
            var Q2;
            {var subQ0=sQuery(id+"F12.wireOp",EDGE,"E11");Q2=makeQuery(id+"F17.boolean.opBoolean","MERGE",EDGE,{"derivedFrom":[makeQuery(id+"F16.boolean.opBoolean","MERGE",EDGE,{"derivedFrom":[makeQuery(id+"F13.opExtrude","CAP_EDGE",EDGE,{"disambiguationData":[OSD([subQ0])],"isStart":false}),makeQuery(id+"F16.opExtrude","SWEPT_EDGE",EDGE,{"disambiguationData":[OSD([sQuery(id+"F10.wireOp",EDGE,"E9.right"),subQ0])]})]}),makeQuery(id+"F17.opExtrude","SWEPT_EDGE",EDGE,{"disambiguationData":[OSD([sQuery(id+"F10.wireOp",EDGE,"E9.left"),subQ0])]})]});}
            var Q3;
            Q3=makeQuery(id+"F17.opExtrude","CAP_EDGE",EDGE,{"disambiguationData":[OSD([sQuery(id+"F10.wireOp",EDGE,"E9.left"),sQuery(id+"F12.wireOp",EDGE,"E11"),sQuery(id+"F14.wireOp",EDGE,"E13")])],"isStart":false});
            var Q4;
            Q4=makeQuery(id+"F13.opExtrude","CAP_EDGE",EDGE,{"disambiguationData":[OSD([sQuery(id+"F12.wireOp",EDGE,"E11")])],"isStart":true});
            var Q5;
            Q5=makeQuery(id+"F13.opExtrude","CAP_EDGE",EDGE,{"disambiguationData":[OSD([sQuery(id+"F12.wireOp",EDGE,"E10")])],"isStart":true});
            var Q6;
            Q6=makeQuery(id+"F23.opExtrude","CAP_EDGE",EDGE,{"disambiguationData":[OSD([sQuery(id+"F22.wireOp",EDGE,"E20")])],"isStart":false});
            var Q7;
            Q7=makeQuery(id+"F25.opExtrude","CAP_EDGE",EDGE,{"disambiguationData":[OSD([sQuery(id+"F24.wireOp",EDGE,"E26")])],"isStart":false});
            var Q8;
            Q8=makeQuery(id+"F25.boolean.opBoolean","MERGE",EDGE,{"derivedFrom":[makeQuery(id+"F16.opExtrude","CAP_EDGE",EDGE,{"disambiguationData":[OSD([sQuery(id+"F10.wireOp",EDGE,"E9.right"),sQuery(id+"F12.wireOp",EDGE,"E10"),sQuery(id+"F15.wireOp",EDGE,"E15")])],"isStart":true}),makeQuery(id+"F25.opExtrude","CAP_EDGE",EDGE,{"disambiguationData":[OSD([sQuery(id+"F24.wireOp",EDGE,"E26")])],"isStart":true})]});
            var Q9;
            Q9=makeQuery(id+"F25.opExtrude","SWEPT_EDGE",EDGE,{"disambiguationData":[OSD([sQuery(id+"F24.wireOp",EDGE,"E25"),sQuery(id+"F24.wireOp",EDGE,"E26")])]});
            var Q10;
            Q10=makeQuery(id+"F23.opExtrude","SWEPT_EDGE",EDGE,{"disambiguationData":[OSD([sQuery(id+"F22.wireOp",EDGE,"E20"),sQuery(id+"F22.wireOp",EDGE,"E21")])]});
            var Q11;
            Q11=makeQuery(id+"F23.boolean.opBoolean","MERGE",EDGE,{"derivedFrom":[makeQuery(id+"F17.opExtrude","CAP_EDGE",EDGE,{"disambiguationData":[OSD([sQuery(id+"F10.wireOp",EDGE,"E9.left"),sQuery(id+"F12.wireOp",EDGE,"E10"),sQuery(id+"F14.wireOp",EDGE,"E12")])],"isStart":true}),makeQuery(id+"F23.opExtrude","CAP_EDGE",EDGE,{"disambiguationData":[OSD([sQuery(id+"F22.wireOp",EDGE,"E20")])],"isStart":true})]});
            var Q12;
            Q12=makeQuery(id+"F16.opExtrude","CAP_EDGE",EDGE,{"disambiguationData":[OSD([sQuery(id+"F10.wireOp",EDGE,"E9.right"),sQuery(id+"F12.wireOp",EDGE,"E10"),sQuery(id+"F15.wireOp",EDGE,"E15")])],"isStart":false});
            var Q13;
            Q13=makeQuery(id+"F17.opExtrude","CAP_EDGE",EDGE,{"disambiguationData":[OSD([sQuery(id+"F10.wireOp",EDGE,"E9.left"),sQuery(id+"F12.wireOp",EDGE,"E10"),sQuery(id+"F14.wireOp",EDGE,"E12")])],"isStart":false});
            var Q14;
            {var subQ0=sQuery(id+"F10.wireOp",EDGE,"E9.left");var subQ1=sQuery(id+"F10.wireOp",EDGE,"E9.bottom");var subQ2=makeQuery(id+"F11.opExtrude","CAP_EDGE",EDGE,{"disambiguationData":[OSD([subQ0])],"isStart":false});var subQ3=makeQuery(id+"F11.opExtrude","CAP_EDGE",EDGE,{"disambiguationData":[OSD([subQ1])],"isStart":false});var subQ5=sQuery(id+"F10.wireOp",EDGE,"E9.right");var subQ6=makeQuery(id+"F11.opExtrude","CAP_EDGE",EDGE,{"disambiguationData":[OSD([subQ5])],"isStart":false});var subQ7=makeQuery(id+"F17.boolean.opBoolean","MERGE",EDGE,{"derivedFrom":[makeQuery(id+"F16.boolean.opBoolean","MERGE",EDGE,{"derivedFrom":[makeQuery(id+"F13.opExtrude","CAP_EDGE",EDGE,{"disambiguationData":[OSD([subQ1])],"isStart":false}),makeQuery(id+"F16.opExtrude","SWEPT_EDGE",EDGE,{"disambiguationData":[OSD([subQ1,subQ5]),TDD([makeQuery(id+"F15.imprint","INTERSECT",VERTEX,{"derivedFrom":[makeQuery(id+"F13.opExtrude","CAP_EDGE",EDGE,{"disambiguationData":[OSD([subQ5]),TDD([makeQuery(id+"F12.imprint","IMPRINT",EDGE,{"disambiguationData":[TD([[makeQuery(id+"F12.imprint","INTERSECT",VERTEX,{"derivedFrom":[subQ3,subQ6]}),-1.0]])],"derivedFrom":subQ6})])],"isStart":false}),makeQuery(id+"F13.boolean.opBoolean","MERGE",EDGE,{"derivedFrom":[makeQuery(id+"F11.opExtrude","SWEPT_EDGE",EDGE,{"disambiguationData":[OSD([subQ1,subQ5])]}),makeQuery(id+"F13.opExtrude","SWEPT_EDGE",EDGE,{"disambiguationData":[OSD([subQ1,subQ5])]})]})]})])]})]}),makeQuery(id+"F17.opExtrude","SWEPT_EDGE",EDGE,{"disambiguationData":[OSD([subQ1,subQ0]),TDD([makeQuery(id+"F14.imprint","INTERSECT",VERTEX,{"derivedFrom":[makeQuery(id+"F13.opExtrude","CAP_EDGE",EDGE,{"disambiguationData":[OSD([subQ0]),TDD([makeQuery(id+"F12.imprint","IMPRINT",EDGE,{"disambiguationData":[TD([[makeQuery(id+"F12.imprint","INTERSECT",VERTEX,{"derivedFrom":[subQ3,subQ2]}),-1.0]])],"derivedFrom":subQ2})])],"isStart":false}),makeQuery(id+"F13.boolean.opBoolean","MERGE",EDGE,{"derivedFrom":[makeQuery(id+"F11.opExtrude","SWEPT_EDGE",EDGE,{"disambiguationData":[OSD([subQ1,subQ0])]}),makeQuery(id+"F13.opExtrude","SWEPT_EDGE",EDGE,{"disambiguationData":[OSD([subQ1,subQ0])]})]})]})])]})]});Q14=makeQuery(id+"F21.opExtrude","CAP_EDGE",EDGE,{"disambiguationData":[OSD([subQ1,subQ0,subQ5]),TDD([makeQuery(id+"F18.imprint","IMPRINT",EDGE,{"disambiguationData":[TD([[makeQuery(id+"F18.imprint","INTERSECT",VERTEX,{"derivedFrom":[subQ7,sQuery(id+"F18.wireOp",EDGE,"E16")]}),-1.0]])],"derivedFrom":subQ7})])],"isStart":false});}
            var Q15;
            {var subQ0=sQuery(id+"F10.wireOp",EDGE,"E9.left");var subQ1=sQuery(id+"F10.wireOp",EDGE,"E9.bottom");var subQ2=makeQuery(id+"F11.opExtrude","CAP_EDGE",EDGE,{"disambiguationData":[OSD([subQ0])],"isStart":false});var subQ3=makeQuery(id+"F11.opExtrude","CAP_EDGE",EDGE,{"disambiguationData":[OSD([subQ1])],"isStart":false});var subQ5=sQuery(id+"F10.wireOp",EDGE,"E9.right");var subQ6=makeQuery(id+"F11.opExtrude","CAP_EDGE",EDGE,{"disambiguationData":[OSD([subQ5])],"isStart":false});var subQ7=makeQuery(id+"F17.boolean.opBoolean","MERGE",EDGE,{"derivedFrom":[makeQuery(id+"F16.boolean.opBoolean","MERGE",EDGE,{"derivedFrom":[makeQuery(id+"F13.opExtrude","CAP_EDGE",EDGE,{"disambiguationData":[OSD([subQ1])],"isStart":false}),makeQuery(id+"F16.opExtrude","SWEPT_EDGE",EDGE,{"disambiguationData":[OSD([subQ1,subQ5]),TDD([makeQuery(id+"F15.imprint","INTERSECT",VERTEX,{"derivedFrom":[makeQuery(id+"F13.opExtrude","CAP_EDGE",EDGE,{"disambiguationData":[OSD([subQ5]),TDD([makeQuery(id+"F12.imprint","IMPRINT",EDGE,{"disambiguationData":[TD([[makeQuery(id+"F12.imprint","INTERSECT",VERTEX,{"derivedFrom":[subQ3,subQ6]}),-1.0]])],"derivedFrom":subQ6})])],"isStart":false}),makeQuery(id+"F13.boolean.opBoolean","MERGE",EDGE,{"derivedFrom":[makeQuery(id+"F11.opExtrude","SWEPT_EDGE",EDGE,{"disambiguationData":[OSD([subQ1,subQ5])]}),makeQuery(id+"F13.opExtrude","SWEPT_EDGE",EDGE,{"disambiguationData":[OSD([subQ1,subQ5])]})]})]})])]})]}),makeQuery(id+"F17.opExtrude","SWEPT_EDGE",EDGE,{"disambiguationData":[OSD([subQ1,subQ0]),TDD([makeQuery(id+"F14.imprint","INTERSECT",VERTEX,{"derivedFrom":[makeQuery(id+"F13.opExtrude","CAP_EDGE",EDGE,{"disambiguationData":[OSD([subQ0]),TDD([makeQuery(id+"F12.imprint","IMPRINT",EDGE,{"disambiguationData":[TD([[makeQuery(id+"F12.imprint","INTERSECT",VERTEX,{"derivedFrom":[subQ3,subQ2]}),-1.0]])],"derivedFrom":subQ2})])],"isStart":false}),makeQuery(id+"F13.boolean.opBoolean","MERGE",EDGE,{"derivedFrom":[makeQuery(id+"F11.opExtrude","SWEPT_EDGE",EDGE,{"disambiguationData":[OSD([subQ1,subQ0])]}),makeQuery(id+"F13.opExtrude","SWEPT_EDGE",EDGE,{"disambiguationData":[OSD([subQ1,subQ0])]})]})]})])]})]});Q15=makeQuery(id+"F21.opExtrude","CAP_EDGE",EDGE,{"disambiguationData":[OSD([subQ1,subQ0,subQ5]),TDD([makeQuery(id+"F18.imprint","IMPRINT",EDGE,{"disambiguationData":[TD([[makeQuery(id+"F18.imprint","INTERSECT",VERTEX,{"derivedFrom":[subQ7,sQuery(id+"F18.wireOp",EDGE,"E17")]}),1.0]])],"derivedFrom":subQ7})])],"isStart":false});}
            var Q16;
            {var subQ0=sQuery(id+"F10.wireOp",EDGE,"E9.left");var subQ1=sQuery(id+"F10.wireOp",EDGE,"E9.bottom");var subQ2=sQuery(id+"F10.wireOp",EDGE,"E9.right");var subQ3=makeQuery(id+"F17.boolean.opBoolean","MERGE",EDGE,{"derivedFrom":[makeQuery(id+"F16.boolean.opBoolean","MERGE",EDGE,{"derivedFrom":[makeQuery(id+"F11.opExtrude","CAP_EDGE",EDGE,{"disambiguationData":[OSD([subQ1])],"isStart":true}),makeQuery(id+"F16.opExtrude","SWEPT_EDGE",EDGE,{"disambiguationData":[OSD([subQ1,subQ2]),TDD([makeQuery(id+"F15.imprint","INTERSECT",VERTEX,{"derivedFrom":[makeQuery(id+"F11.opExtrude","CAP_EDGE",EDGE,{"disambiguationData":[OSD([subQ2])],"isStart":true}),makeQuery(id+"F13.boolean.opBoolean","MERGE",EDGE,{"derivedFrom":[makeQuery(id+"F11.opExtrude","SWEPT_EDGE",EDGE,{"disambiguationData":[OSD([subQ1,subQ2])]}),makeQuery(id+"F13.opExtrude","SWEPT_EDGE",EDGE,{"disambiguationData":[OSD([subQ1,subQ2])]})]})]})])]})]}),makeQuery(id+"F17.opExtrude","SWEPT_EDGE",EDGE,{"disambiguationData":[OSD([subQ1,subQ0]),TDD([makeQuery(id+"F14.imprint","INTERSECT",VERTEX,{"derivedFrom":[makeQuery(id+"F11.opExtrude","CAP_EDGE",EDGE,{"disambiguationData":[OSD([subQ0])],"isStart":true}),makeQuery(id+"F13.boolean.opBoolean","MERGE",EDGE,{"derivedFrom":[makeQuery(id+"F11.opExtrude","SWEPT_EDGE",EDGE,{"disambiguationData":[OSD([subQ1,subQ0])]}),makeQuery(id+"F13.opExtrude","SWEPT_EDGE",EDGE,{"disambiguationData":[OSD([subQ1,subQ0])]})]})]})])]})]});Q16=makeQuery(id+"F21.opExtrude","CAP_EDGE",EDGE,{"disambiguationData":[OSD([subQ1,subQ0,subQ2]),TDD([makeQuery(id+"F18.imprint","IMPRINT",EDGE,{"disambiguationData":[TD([[makeQuery(id+"F18.imprint","INTERSECT",VERTEX,{"derivedFrom":[subQ3,sQuery(id+"F18.wireOp",EDGE,"E17")]}),1.0]])],"derivedFrom":subQ3})])],"isStart":false});}
            var Q17;
            {var subQ0=sQuery(id+"F10.wireOp",EDGE,"E9.left");var subQ1=sQuery(id+"F10.wireOp",EDGE,"E9.bottom");var subQ2=sQuery(id+"F10.wireOp",EDGE,"E9.right");var subQ3=makeQuery(id+"F17.boolean.opBoolean","MERGE",EDGE,{"derivedFrom":[makeQuery(id+"F16.boolean.opBoolean","MERGE",EDGE,{"derivedFrom":[makeQuery(id+"F11.opExtrude","CAP_EDGE",EDGE,{"disambiguationData":[OSD([subQ1])],"isStart":true}),makeQuery(id+"F16.opExtrude","SWEPT_EDGE",EDGE,{"disambiguationData":[OSD([subQ1,subQ2]),TDD([makeQuery(id+"F15.imprint","INTERSECT",VERTEX,{"derivedFrom":[makeQuery(id+"F11.opExtrude","CAP_EDGE",EDGE,{"disambiguationData":[OSD([subQ2])],"isStart":true}),makeQuery(id+"F13.boolean.opBoolean","MERGE",EDGE,{"derivedFrom":[makeQuery(id+"F11.opExtrude","SWEPT_EDGE",EDGE,{"disambiguationData":[OSD([subQ1,subQ2])]}),makeQuery(id+"F13.opExtrude","SWEPT_EDGE",EDGE,{"disambiguationData":[OSD([subQ1,subQ2])]})]})]})])]})]}),makeQuery(id+"F17.opExtrude","SWEPT_EDGE",EDGE,{"disambiguationData":[OSD([subQ1,subQ0]),TDD([makeQuery(id+"F14.imprint","INTERSECT",VERTEX,{"derivedFrom":[makeQuery(id+"F11.opExtrude","CAP_EDGE",EDGE,{"disambiguationData":[OSD([subQ0])],"isStart":true}),makeQuery(id+"F13.boolean.opBoolean","MERGE",EDGE,{"derivedFrom":[makeQuery(id+"F11.opExtrude","SWEPT_EDGE",EDGE,{"disambiguationData":[OSD([subQ1,subQ0])]}),makeQuery(id+"F13.opExtrude","SWEPT_EDGE",EDGE,{"disambiguationData":[OSD([subQ1,subQ0])]})]})]})])]})]});Q17=makeQuery(id+"F21.opExtrude","CAP_EDGE",EDGE,{"disambiguationData":[OSD([subQ1,subQ0,subQ2]),TDD([makeQuery(id+"F18.imprint","IMPRINT",EDGE,{"disambiguationData":[TD([[makeQuery(id+"F18.imprint","INTERSECT",VERTEX,{"derivedFrom":[subQ3,sQuery(id+"F18.wireOp",EDGE,"E16")]}),-1.0]])],"derivedFrom":subQ3})])],"isStart":false});}
            var Q18;
            {var subQ0=sQuery(id+"F10.wireOp",EDGE,"E9.left");var subQ1=sQuery(id+"F10.wireOp",EDGE,"E9.top");var subQ2=makeQuery(id+"F11.opExtrude","CAP_EDGE",EDGE,{"disambiguationData":[OSD([subQ0])],"isStart":false});var subQ3=makeQuery(id+"F11.opExtrude","CAP_EDGE",EDGE,{"disambiguationData":[OSD([subQ1])],"isStart":false});var subQ5=sQuery(id+"F10.wireOp",EDGE,"E9.right");var subQ6=makeQuery(id+"F11.opExtrude","CAP_EDGE",EDGE,{"disambiguationData":[OSD([subQ5])],"isStart":false});var subQ7=makeQuery(id+"F17.boolean.opBoolean","MERGE",EDGE,{"derivedFrom":[makeQuery(id+"F16.boolean.opBoolean","MERGE",EDGE,{"derivedFrom":[makeQuery(id+"F13.opExtrude","CAP_EDGE",EDGE,{"disambiguationData":[OSD([subQ1])],"isStart":false}),makeQuery(id+"F16.opExtrude","SWEPT_EDGE",EDGE,{"disambiguationData":[OSD([subQ1,subQ5]),TDD([makeQuery(id+"F15.imprint","INTERSECT",VERTEX,{"derivedFrom":[makeQuery(id+"F13.opExtrude","CAP_EDGE",EDGE,{"disambiguationData":[OSD([subQ5]),TDD([makeQuery(id+"F12.imprint","IMPRINT",EDGE,{"disambiguationData":[TD([[makeQuery(id+"F12.imprint","INTERSECT",VERTEX,{"derivedFrom":[subQ3,subQ6]}),1.0]])],"derivedFrom":subQ6})])],"isStart":false}),makeQuery(id+"F13.boolean.opBoolean","MERGE",EDGE,{"derivedFrom":[makeQuery(id+"F11.opExtrude","SWEPT_EDGE",EDGE,{"disambiguationData":[OSD([subQ1,subQ5])]}),makeQuery(id+"F13.opExtrude","SWEPT_EDGE",EDGE,{"disambiguationData":[OSD([subQ1,subQ5])]})]})]})])]})]}),makeQuery(id+"F17.opExtrude","SWEPT_EDGE",EDGE,{"disambiguationData":[OSD([subQ1,subQ0]),TDD([makeQuery(id+"F14.imprint","INTERSECT",VERTEX,{"derivedFrom":[makeQuery(id+"F13.opExtrude","CAP_EDGE",EDGE,{"disambiguationData":[OSD([subQ0]),TDD([makeQuery(id+"F12.imprint","IMPRINT",EDGE,{"disambiguationData":[TD([[makeQuery(id+"F12.imprint","INTERSECT",VERTEX,{"derivedFrom":[subQ3,subQ2]}),1.0]])],"derivedFrom":subQ2})])],"isStart":false}),makeQuery(id+"F13.boolean.opBoolean","MERGE",EDGE,{"derivedFrom":[makeQuery(id+"F11.opExtrude","SWEPT_EDGE",EDGE,{"disambiguationData":[OSD([subQ1,subQ0])]}),makeQuery(id+"F13.opExtrude","SWEPT_EDGE",EDGE,{"disambiguationData":[OSD([subQ1,subQ0])]})]})]})])]})]});Q18=makeQuery(id+"F20.opExtrude","CAP_EDGE",EDGE,{"disambiguationData":[OSD([subQ1,subQ0,subQ5]),TDD([makeQuery(id+"F19.imprint","IMPRINT",EDGE,{"disambiguationData":[TD([[makeQuery(id+"F19.imprint","INTERSECT",VERTEX,{"derivedFrom":[subQ7,sQuery(id+"F19.wireOp",EDGE,"E18")]}),1.0]])],"derivedFrom":subQ7})])],"isStart":false});}
            var Q19;
            {var subQ0=sQuery(id+"F10.wireOp",EDGE,"E9.left");var subQ1=sQuery(id+"F10.wireOp",EDGE,"E9.top");var subQ2=makeQuery(id+"F11.opExtrude","CAP_EDGE",EDGE,{"disambiguationData":[OSD([subQ0])],"isStart":false});var subQ3=makeQuery(id+"F11.opExtrude","CAP_EDGE",EDGE,{"disambiguationData":[OSD([subQ1])],"isStart":false});var subQ5=sQuery(id+"F10.wireOp",EDGE,"E9.right");var subQ6=makeQuery(id+"F11.opExtrude","CAP_EDGE",EDGE,{"disambiguationData":[OSD([subQ5])],"isStart":false});var subQ7=makeQuery(id+"F17.boolean.opBoolean","MERGE",EDGE,{"derivedFrom":[makeQuery(id+"F16.boolean.opBoolean","MERGE",EDGE,{"derivedFrom":[makeQuery(id+"F13.opExtrude","CAP_EDGE",EDGE,{"disambiguationData":[OSD([subQ1])],"isStart":false}),makeQuery(id+"F16.opExtrude","SWEPT_EDGE",EDGE,{"disambiguationData":[OSD([subQ1,subQ5]),TDD([makeQuery(id+"F15.imprint","INTERSECT",VERTEX,{"derivedFrom":[makeQuery(id+"F13.opExtrude","CAP_EDGE",EDGE,{"disambiguationData":[OSD([subQ5]),TDD([makeQuery(id+"F12.imprint","IMPRINT",EDGE,{"disambiguationData":[TD([[makeQuery(id+"F12.imprint","INTERSECT",VERTEX,{"derivedFrom":[subQ3,subQ6]}),1.0]])],"derivedFrom":subQ6})])],"isStart":false}),makeQuery(id+"F13.boolean.opBoolean","MERGE",EDGE,{"derivedFrom":[makeQuery(id+"F11.opExtrude","SWEPT_EDGE",EDGE,{"disambiguationData":[OSD([subQ1,subQ5])]}),makeQuery(id+"F13.opExtrude","SWEPT_EDGE",EDGE,{"disambiguationData":[OSD([subQ1,subQ5])]})]})]})])]})]}),makeQuery(id+"F17.opExtrude","SWEPT_EDGE",EDGE,{"disambiguationData":[OSD([subQ1,subQ0]),TDD([makeQuery(id+"F14.imprint","INTERSECT",VERTEX,{"derivedFrom":[makeQuery(id+"F13.opExtrude","CAP_EDGE",EDGE,{"disambiguationData":[OSD([subQ0]),TDD([makeQuery(id+"F12.imprint","IMPRINT",EDGE,{"disambiguationData":[TD([[makeQuery(id+"F12.imprint","INTERSECT",VERTEX,{"derivedFrom":[subQ3,subQ2]}),1.0]])],"derivedFrom":subQ2})])],"isStart":false}),makeQuery(id+"F13.boolean.opBoolean","MERGE",EDGE,{"derivedFrom":[makeQuery(id+"F11.opExtrude","SWEPT_EDGE",EDGE,{"disambiguationData":[OSD([subQ1,subQ0])]}),makeQuery(id+"F13.opExtrude","SWEPT_EDGE",EDGE,{"disambiguationData":[OSD([subQ1,subQ0])]})]})]})])]})]});Q19=makeQuery(id+"F20.opExtrude","CAP_EDGE",EDGE,{"disambiguationData":[OSD([subQ1,subQ0,subQ5]),TDD([makeQuery(id+"F19.imprint","IMPRINT",EDGE,{"disambiguationData":[TD([[makeQuery(id+"F19.imprint","INTERSECT",VERTEX,{"derivedFrom":[subQ7,sQuery(id+"F19.wireOp",EDGE,"E19")]}),-1.0]])],"derivedFrom":subQ7})])],"isStart":false});}
            var Q20;
            {var subQ0=sQuery(id+"F10.wireOp",EDGE,"E9.left");var subQ1=sQuery(id+"F10.wireOp",EDGE,"E9.top");var subQ2=sQuery(id+"F10.wireOp",EDGE,"E9.right");var subQ3=makeQuery(id+"F17.boolean.opBoolean","MERGE",EDGE,{"derivedFrom":[makeQuery(id+"F16.boolean.opBoolean","MERGE",EDGE,{"derivedFrom":[makeQuery(id+"F11.opExtrude","CAP_EDGE",EDGE,{"disambiguationData":[OSD([subQ1])],"isStart":true}),makeQuery(id+"F16.opExtrude","SWEPT_EDGE",EDGE,{"disambiguationData":[OSD([subQ1,subQ2]),TDD([makeQuery(id+"F15.imprint","INTERSECT",VERTEX,{"derivedFrom":[makeQuery(id+"F11.opExtrude","CAP_EDGE",EDGE,{"disambiguationData":[OSD([subQ2])],"isStart":true}),makeQuery(id+"F13.boolean.opBoolean","MERGE",EDGE,{"derivedFrom":[makeQuery(id+"F11.opExtrude","SWEPT_EDGE",EDGE,{"disambiguationData":[OSD([subQ1,subQ2])]}),makeQuery(id+"F13.opExtrude","SWEPT_EDGE",EDGE,{"disambiguationData":[OSD([subQ1,subQ2])]})]})]})])]})]}),makeQuery(id+"F17.opExtrude","SWEPT_EDGE",EDGE,{"disambiguationData":[OSD([subQ1,subQ0]),TDD([makeQuery(id+"F14.imprint","INTERSECT",VERTEX,{"derivedFrom":[makeQuery(id+"F11.opExtrude","CAP_EDGE",EDGE,{"disambiguationData":[OSD([subQ0])],"isStart":true}),makeQuery(id+"F13.boolean.opBoolean","MERGE",EDGE,{"derivedFrom":[makeQuery(id+"F11.opExtrude","SWEPT_EDGE",EDGE,{"disambiguationData":[OSD([subQ1,subQ0])]}),makeQuery(id+"F13.opExtrude","SWEPT_EDGE",EDGE,{"disambiguationData":[OSD([subQ1,subQ0])]})]})]})])]})]});Q20=makeQuery(id+"F20.opExtrude","CAP_EDGE",EDGE,{"disambiguationData":[OSD([subQ1,subQ0,subQ2]),TDD([makeQuery(id+"F19.imprint","IMPRINT",EDGE,{"disambiguationData":[TD([[makeQuery(id+"F19.imprint","INTERSECT",VERTEX,{"derivedFrom":[subQ3,sQuery(id+"F19.wireOp",EDGE,"E18")]}),1.0]])],"derivedFrom":subQ3})])],"isStart":false});}
            chamfer(context, id + "F29", {"entities" : qUnion([Q0, Q1, Q2, Q3, Q4, Q5, Q6, Q7, Q8, Q9, Q10, Q11, Q12, Q13, Q14, Q15, Q16, Q17, Q18, Q19, Q20]), "width" : 2 * mm, "tangentPropagation" : true});
        }
        {
            var Q0;
            Q0=makeQuery(id+"F1.opExtrude","SWEPT_BODY",BODY,{"disambiguationData":[OSD([sQuery(id+"F0.wireOp",EDGE,"E1.bottom"),sQuery(id+"F0.wireOp",EDGE,"E1.top"),sQuery(id+"F0.wireOp",EDGE,"E1.left"),sQuery(id+"F0.wireOp",EDGE,"E1.right")])]});
            deleteBodies(context, id + "F30", {"entities" : qUnion([Q0])});
        }
    });
